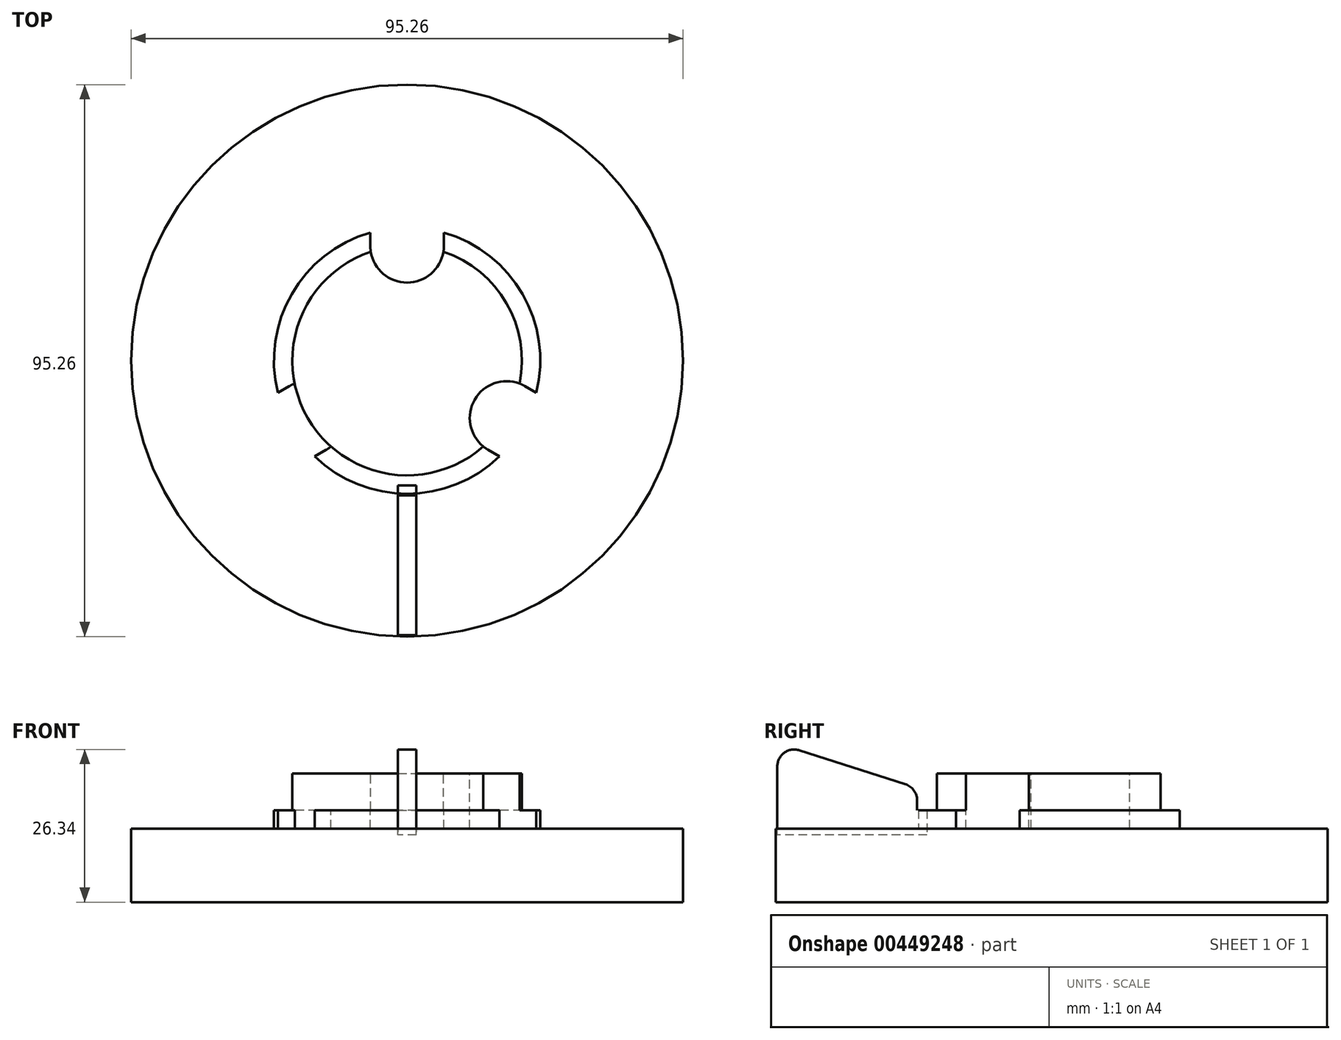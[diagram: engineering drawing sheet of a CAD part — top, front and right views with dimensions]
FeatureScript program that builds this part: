
annotation { "Feature Type Name" : "Feature", "Feature Type Description" : "" }
export const myFeature = defineFeature(function(context is Context, id is Id, definition is map)
    precondition{}
    {
        {
            var Q0;
            Q0=qCreatedBy(makeId("Top.planeOp"),FACE);
            var sketch = newSketch(context, id + "F0", { "sketchPlane" : qUnion([Q0])});
            skCircle(sketch, "E0", {"center": v(0, 0) * mm, "radius": 47.63 * mm});
            skSolve(sketch);
        }
        {
            var Q0;
            Q0=makeQuery(id+"F0.imprint","IMPRINT",FACE,{"disambiguationData":[TD([[makeQuery(id+"F0.imprint","IMPRINT",EDGE,{"derivedFrom":sQuery(id+"F0.wireOp",EDGE,"E0")}),1.0]])]});
            extrude(context, id + "F1", {"entities" : qUnion([Q0]), "depth" : 12.7 * mm});
        }
        {
            var Q0;
            Q0=makeQuery(id+"F1.opExtrude","CAP_FACE",FACE,{"disambiguationData":[OSD([sQuery(id+"F0.wireOp",EDGE,"E0")])],"isStart":false});
            var sketch = newSketch(context, id + "F2", { "sketchPlane" : qUnion([Q0])});
            skCircle(sketch, "E1", {"center": v(0, 0) * mm, "radius": 19.81 * mm});
            skSolve(sketch);
        }
        {
            var Q0;
            Q0=makeQuery(id+"F2.imprint","IMPRINT",FACE,{"disambiguationData":[TD([[makeQuery(id+"F2.imprint","IMPRINT",EDGE,{"derivedFrom":sQuery(id+"F2.wireOp",EDGE,"E1")}),1.0]])]});
            extrude(context, id + "F3", {"entities" : qUnion([Q0]), "operationType" : NewBodyOperationType.ADD, "depth" : 9.52 * mm});
        }
        {
            var Q0;
            Q0=makeQuery(id+"F1.opExtrude","CAP_FACE",FACE,{"disambiguationData":[OSD([sQuery(id+"F0.wireOp",EDGE,"E0")])],"isStart":false});
            var sketch = newSketch(context, id + "F4", { "sketchPlane" : qUnion([Q0])});
            skCircle(sketch, "E2", {"center": v(0, 0) * mm, "radius": 22.99 * mm});
            skSolve(sketch);
        }
        {
            var Q0;
            Q0=makeQuery(id+"F4.imprint","IMPRINT",FACE,{"disambiguationData":[TD([[makeQuery(id+"F4.imprint","IMPRINT",EDGE,{"derivedFrom":sQuery(id+"F4.wireOp",EDGE,"E2")}),1.0]])]});
            extrude(context, id + "F5", {"entities" : qUnion([Q0]), "operationType" : NewBodyOperationType.ADD, "depth" : 3.17 * mm});
        }
        {
            var Q0;
            Q0=makeQuery(id+"F3.opExtrude","CAP_FACE",FACE,{"disambiguationData":[OSD([sQuery(id+"F2.wireOp",EDGE,"E1")])],"isStart":false});
            var sketch = newSketch(context, id + "F6", { "sketchPlane" : qUnion([Q0])});
            skArc(sketch, "E3", {"start": v(20.33, -4.4) * mm, "mid": v(11.66, -6.73) * mm, "end": v(13.98, -15.4) * mm});
            skLineSegment(sketch, "E4", {"start": v(13.98, -15.4) * mm, "end": v(15.96, -16.55) * mm});
            skLineSegment(sketch, "E5", {"start": v(22.3, -5.55) * mm, "end": v(20.33, -4.4) * mm});
            skArc(sketch, "E6.0", {"start": v(15.96, -16.55) * mm, "mid": v(19.9, -11.5) * mm, "end": v(22.3, -5.55) * mm});
            skArc(sketch, "E7.1.0", {"start": v(-6.35, 19.81) * mm, "mid": v(0, 13.46) * mm, "end": v(6.35, 19.81) * mm});
            skLineSegment(sketch, "E7.1.1", {"start": v(6.35, 19.81) * mm, "end": v(6.35, 22.1) * mm});
            skArc(sketch, "E7.1.2", {"start": v(6.35, 22.1) * mm, "mid": v(0, 22.99) * mm, "end": v(-6.35, 22.1) * mm});
            skLineSegment(sketch, "E7.1.3", {"start": v(-6.35, 22.1) * mm, "end": v(-6.35, 19.81) * mm});
            skArc(sketch, "E7.2.0", {"start": v(-13.98, -15.4) * mm, "mid": v(-11.66, -6.73) * mm, "end": v(-20.33, -4.4) * mm});
            skLineSegment(sketch, "E7.2.1", {"start": v(-20.33, -4.4) * mm, "end": v(-22.3, -5.55) * mm});
            skArc(sketch, "E7.2.2", {"start": v(-22.3, -5.55) * mm, "mid": v(-19.9, -11.5) * mm, "end": v(-15.96, -16.55) * mm});
            skLineSegment(sketch, "E7.2.3", {"start": v(-15.96, -16.55) * mm, "end": v(-13.98, -15.4) * mm});
            skSolve(sketch);
        }
        {
            var Q0;
            {var subQ1=sQuery(id+"F6.wireOp",EDGE,"E4");Q0=makeQuery(id+"F6.imprint","IMPRINT",FACE,{"disambiguationData":[TD([[makeQuery(id+"F6.imprint","IMPRINT",EDGE,{"derivedFrom":subQ1}),1.0]])]});}
            var Q1;
            {var subQ0=sQuery(id+"F6.wireOp",EDGE,"E3");var subQ1=makeQuery(id+"F3.opExtrude","CAP_EDGE",EDGE,{"disambiguationData":[OSD([sQuery(id+"F2.wireOp",EDGE,"E1")])],"isStart":false});var subQ2=makeQuery(id+"F6.imprint","INTERSECT",VERTEX,{"disambiguationData":[OD(0.0)],"derivedFrom":[subQ1,subQ0]});Q1=makeQuery(id+"F6.imprint","IMPRINT",FACE,{"disambiguationData":[TD([[makeQuery(id+"F6.imprint","IMPRINT",EDGE,{"disambiguationData":[TD([[subQ2,-1.0]])],"derivedFrom":subQ0}),1.0]])]});}
            var Q2;
            {var subQ0=sQuery(id+"F6.wireOp",EDGE,"E7.2.1");Q2=makeQuery(id+"F6.imprint","IMPRINT",FACE,{"disambiguationData":[TD([[makeQuery(id+"F6.imprint","IMPRINT",EDGE,{"derivedFrom":subQ0}),1.0]])]});}
            var Q3;
            {var subQ0=sQuery(id+"F6.wireOp",EDGE,"E7.2.0");var subQ1=makeQuery(id+"F3.opExtrude","CAP_EDGE",EDGE,{"disambiguationData":[OSD([sQuery(id+"F2.wireOp",EDGE,"E1")])],"isStart":false});var subQ2=makeQuery(id+"F6.imprint","INTERSECT",VERTEX,{"disambiguationData":[OD(0.0)],"derivedFrom":[subQ1,subQ0]});Q3=makeQuery(id+"F6.imprint","IMPRINT",FACE,{"disambiguationData":[TD([[makeQuery(id+"F6.imprint","IMPRINT",EDGE,{"disambiguationData":[TD([[subQ2,-1.0]])],"derivedFrom":subQ0}),1.0]])]});}
            var Q4;
            {var subQ0=sQuery(id+"F6.wireOp",EDGE,"E7.1.0");var subQ1=makeQuery(id+"F3.opExtrude","CAP_EDGE",EDGE,{"disambiguationData":[OSD([sQuery(id+"F2.wireOp",EDGE,"E1")])],"isStart":false});var subQ2=makeQuery(id+"F6.imprint","INTERSECT",VERTEX,{"disambiguationData":[OD(0.0)],"derivedFrom":[subQ1,subQ0]});Q4=makeQuery(id+"F6.imprint","IMPRINT",FACE,{"disambiguationData":[TD([[makeQuery(id+"F6.imprint","IMPRINT",EDGE,{"disambiguationData":[TD([[subQ2,-1.0]])],"derivedFrom":subQ0}),1.0]])]});}
            var Q5;
            {var subQ0=sQuery(id+"F6.wireOp",EDGE,"E7.1.1");Q5=makeQuery(id+"F6.imprint","IMPRINT",FACE,{"disambiguationData":[TD([[makeQuery(id+"F6.imprint","IMPRINT",EDGE,{"derivedFrom":subQ0}),1.0]])]});}
            var Q6;
            Q6=makeQuery(id+"F1.opExtrude","CAP_FACE",FACE,{"disambiguationData":[OSD([sQuery(id+"F0.wireOp",EDGE,"E0")])],"isStart":false});
            extrude(context, id + "F7", {"entities" : qUnion([Q0, Q1, Q2, Q3, Q4, Q5]), "operationType" : NewBodyOperationType.REMOVE, "endBound" : BoundingType.UP_TO_SURFACE, "oppositeDirection" : true, "endBoundEntityFace" : qUnion([Q6]), "depth" : 25.4 * mm});
        }
        {
            var Q0;
            Q0=qCreatedBy(makeId("Right.planeOp"),FACE);
            var sketch = newSketch(context, id + "F8", { "sketchPlane" : qUnion([Q0])});
            skLineSegment(sketch, "E8", {"start": v(-21.52, 15.88) * mm, "end": v(-21.52, 11.58) * mm});
            skLineSegment(sketch, "E9", {"start": v(-21.52, 11.58) * mm, "end": v(-47.37, 11.58) * mm});
            skLineSegment(sketch, "E10.0", {"start": v(-21.52, 15.88) * mm, "end": v(-23.24, 15.88) * mm});
            skPoint(sketch, "E11.orphan", {"position": v(-16.55, 15.88) * mm});
            skLineSegment(sketch, "E12.0", {"start": v(-47.37, 11.58) * mm, "end": v(-47.37, 23.42) * mm});
            skLineSegment(sketch, "E13.0", {"start": v(-25.27, 20.36) * mm, "end": v(-43.56, 26.2) * mm});
            skArc(sketch, "E14", {"start": v(-43.56, 26.2) * mm, "mid": v(-46.17, 25.78) * mm, "end": v(-47.37, 23.42) * mm});
            skArc(sketch, "E15", {"start": v(-23.24, 17.57) * mm, "mid": v(-23.8, 19.3) * mm, "end": v(-25.27, 20.36) * mm});
            skLineSegment(sketch, "E16", {"start": v(-23.24, 17.57) * mm, "end": v(-23.24, 15.88) * mm});
            skSolve(sketch);
        }
        {
            var Q0;
            Q0=makeQuery(id+"F8.imprint","IMPRINT",FACE,{"disambiguationData":[TD([[makeQuery(id+"F8.imprint","IMPRINT",EDGE,{"derivedFrom":sQuery(id+"F8.wireOp",EDGE,"E8")}),-1.0]])]});
            extrude(context, id + "F9", {"entities" : qUnion([Q0]), "endBound" : BoundingType.SYMMETRIC, "depth" : 3.17 * mm});
        }
    });
